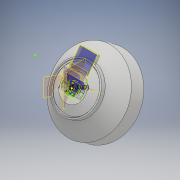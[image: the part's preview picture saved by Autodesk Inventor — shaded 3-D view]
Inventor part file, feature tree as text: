
AUTODESK INVENTOR PART (.ipt)
format: ipt  version: 2018 (Build 220112000, 112)  size: 3,336,704 bytes
history: native  units: mm
features: sketch x136, extrude x121, fillet x44, plane x12, revolve x5, hole x1, direct_edit x1, other x1
ambient origin geometry x8: Origin, YZ Plane, XZ Plane, XY Plane, X Axis, Y Axis, Z Axis, Center Point
bodies: Body1 (feature_tree)
feature tree (321):
  plane  "Work Plane5"
  sketch  "Sketch28"  dims[d118=18.7mm d119=0.0mm d120=0.9mm d121=0.0mm]
  extrude  "Extrusion21"  Depth=0.9mm TaperAngle=0.0deg
  plane  "Work Plane4"
  extrude  "Extrusion22"  Depth=3.8mm
  extrude  "Extrusion23"  Depth=46.7mm
  plane  "Work Plane3"
  hole  "Hole6"  [1 undecoded]
  extrude  "Extrusion27"  Depth=3.8mm
  extrude  "Extrusion28"  Depth=32.03mm
  extrude  "Extrusion30"  Depth=10.0mm TaperAngle=0.0deg
  extrude  "Extrusion31"  Depth=16.3mm TaperAngle=0.0deg
  sketch  "Sketch56"  dims[d188=16.3mm d189=0.0mm d190=16.3mm d191=0.0mm]
  sketch  "Sketch57"  dims[d192=16.3mm d193=0.0mm d194=16.3mm d195=0.0mm]
  extrude  "Extrusion33"  Depth=16.3mm TaperAngle=0.0deg
  extrude  "Extrusion34"  Depth=16.3mm TaperAngle=0.0deg
  extrude  "Extrusion35"  Depth=15.9mm TaperAngle=0.0deg
  extrude  "Extrusion36"  Depth=15.9mm TaperAngle=0.0deg
  extrude  "Extrusion37"  TaperAngle=90.0deg  [1 undecoded]
  extrude  "Extrusion38"  TaperAngle=0.0deg  [1 undecoded]
  extrude  "Extrusion39"  Depth=0.2mm TaperAngle=0.0deg
  extrude  "Extrusion40"  Depth=3.17mm
  extrude  "Extrusion41"  Depth=6.1mm
  sketch  "Sketch68"  dims[d251=10.0mm d252=0.0mm d253=3.91mm d254=0.0mm]
  sketch  "Sketch69"  dims[d255=0.0mm d256=0.0mm d257=3.91mm d258=0.0mm]
  extrude  "Extrusion42"  Depth=0.8mm TaperAngle=0.0deg
  extrude  "Extrusion43"  TaperAngle=0.0deg  [1 undecoded]
  extrude  "Extrusion45"  Depth=10.0mm TaperAngle=0.0deg
  extrude  "Extrusion47"  Depth=3.91mm TaperAngle=0.0deg
  extrude  "Extrusion48"  Depth=0.6mm TaperAngle=0.0deg
  extrude  "Extrusion49"  Depth=0.199mm
  direct_edit  "Direct Edit3"
  extrude  "Extrusion51"  TaperAngle=0.0deg  [1 undecoded]
  extrude  "Extrusion52"  Depth=0.7mm TaperAngle=0.0deg
  extrude  "Extrusion53"  Depth=0.09mm TaperAngle=0.0deg
  extrude  "Extrusion54"  TaperAngle=0.0deg  [1 undecoded]
  extrude  "Extrusion55"  Depth=3.9mm TaperAngle=0.0deg
  extrude  "Extrusion60"  TaperAngle=0.0deg  [1 undecoded]
  extrude  "Extrusion61"  Depth=0.657mm
  extrude  "Extrusion62"  Depth=10.0mm TaperAngle=0.0deg
  fillet  "Fillet13"  Radius=10.0mm
  extrude  "Extrusion64"  TaperAngle=0.0deg  [1 undecoded]
  extrude  "Extrusion65"  TaperAngle=0.0deg  [1 undecoded]
  extrude  "Extrusion66"  Depth=0.253mm
  extrude  "Extrusion67"  TaperAngle=0.0deg  [1 undecoded]
  fillet  "Fillet14"  [1 undecoded]
  extrude  "Extrusion68"  Depth=15.0mm
  extrude  "Extrusion69"  Depth=22.68928mm
  extrude  "Extrusion70"  TaperAngle=90.0deg  [1 undecoded]
  fillet  "Fillet15"  [1 undecoded]
  extrude  "Extrusion71"  TaperAngle=90.0deg  [1 undecoded]
  extrude  "Extrusion72"  Depth=3.490659mm
  extrude  "Extrusion73"  Depth=2.0mm TaperAngle=0.0deg
  extrude  "Extrusion74"  TaperAngle=0.0deg  [1 undecoded]
  fillet  "Fillet16"  Radius=10.0mm
  fillet  "Fillet17"  Radius=0.22mm
  extrude  "Extrusion75"  Depth=5.0mm TaperAngle=0.0deg
  plane  "Work Plane6"
  extrude  "Extrusion78"  Depth=10.0mm TaperAngle=0.0deg
  extrude  "Extrusion79"  Depth=10.0mm TaperAngle=0.0deg
  extrude  "Extrusion80"  Depth=10.0mm TaperAngle=0.0deg
  extrude  "Extrusion81"  Depth=10.0mm TaperAngle=0.0deg
  extrude  "Extrusion82"  Depth=10.0mm
  fillet  "Fillet18"  [1 undecoded]
  fillet  "Fillet19"  Radius=5.99mm
  fillet  "Fillet20"  Radius=1.49mm
  extrude  "Extrusion83"  Depth=1.77mm
  extrude  "Extrusion84"  Depth=10.0mm TaperAngle=0.0deg
  fillet  "Fillet21"  Radius=4.0mm
  extrude  "Extrusion87"  Depth=4.0mm TaperAngle=0.0deg
  plane  "Work Plane7"
  extrude  "Extrusion88"  TaperAngle=0.0deg  [1 undecoded]
  extrude  "Extrusion89"  Depth=7.0mm TaperAngle=0.0deg
  extrude  "Extrusion90"  Depth=10.0mm TaperAngle=0.0deg
  extrude  "Extrusion91"  Depth=7.0mm TaperAngle=0.0deg
  fillet  "Fillet27"  Radius=7.0mm
  extrude  "Extrusion93"  Depth=7.0mm TaperAngle=0.0deg
  extrude  "Extrusion94"  Depth=1.7mm TaperAngle=0.0deg
  fillet  "Fillet29"  [1 undecoded]
  extrude  "Extrusion95"  Depth=10.0mm TaperAngle=0.0deg
  extrude  "Extrusion97"  Depth=10.0mm TaperAngle=0.0deg
  extrude  "Extrusion98"  Depth=1.0mm TaperAngle=0.0deg
  extrude  "Extrusion99"  Depth=15.687mm
  extrude  "Extrusion100"  Depth=9.4mm
  extrude  "Extrusion101"  TaperAngle=90.0deg  [1 undecoded]
  extrude  "Extrusion102"  Depth=10.0mm TaperAngle=0.0deg
  extrude  "Extrusion104"  Depth=50.0mm TaperAngle=0.0deg
  fillet  "Fillet30"  Radius=50.0mm
  extrude  "Extrusion106"  Depth=10.0mm TaperAngle=0.0deg
  fillet  "Fillet33"  Radius=32.0mm
  fillet  "Fillet34"  Radius=9.4mm
  fillet  "Fillet35"  [1 undecoded]
  fillet  "Fillet38"  Radius=10.0mm
  extrude  "Extrusion108"  Depth=10.0mm TaperAngle=0.0deg
  extrude  "Extrusion109"  Depth=10.0mm TaperAngle=0.0deg
  extrude  "Extrusion110"  TaperAngle=0.0deg  [1 undecoded]
  extrude  "Extrusion111"  Depth=18.0mm TaperAngle=0.0deg
  extrude  "Extrusion112"  Depth=2.0mm
  sketch  "Sketch146"  dims[d571=2.0mm d572=2.0mm]
  extrude  "Extrusion113"  Depth=2.0mm
  extrude  "Extrusion114"  Depth=2.0mm
  extrude  "Extrusion115"  Depth=2.0mm
  extrude  "Extrusion116"  Depth=2.0mm
  extrude  "Extrusion118"  Depth=2.0mm
  sketch  "Sketch154"  dims[d590=2.0mm d591=4.0mm]
  extrude  "Extrusion119"  Depth=2.0mm
  extrude  "Extrusion120"  Depth=0.7mm TaperAngle=0.0deg
  extrude  "Extrusion121"  Depth=10.0mm TaperAngle=0.0deg
  extrude  "Extrusion122"  Depth=17.0mm TaperAngle=0.0deg
  extrude  "Extrusion123"  Depth=4.0mm
  extrude  "Extrusion124"  Depth=1.0mm TaperAngle=0.0deg
  extrude  "Extrusion125"  Depth=6.6945mm
  extrude  "Extrusion126"  TaperAngle=0.0deg  [1 undecoded]
  extrude  "Extrusion128"  Depth=15.2mm
  extrude  "Extrusion129"  Depth=26.0mm
  extrude  "Extrusion130"  Depth=28.5mm TaperAngle=0.0deg
  plane  "Work Plane9"
  extrude  "Extrusion133"  Depth=2.0mm
  extrude  "Extrusion134"  Depth=0.567mm
  plane  "Work Plane8"
  extrude  "Extrusion135"  Depth=0.37mm TaperAngle=0.0deg
  plane  "Work Plane2"
  revolve  "Revolution3"  [1 undecoded]
  plane  "Work Plane10"
  extrude  "Extrusion136"  Depth=2.0mm
  extrude  "Extrusion137"  Depth=2.0mm
  extrude  "Extrusion138"  TaperAngle=90.0deg  [1 undecoded]
  extrude  "Extrusion139"  Depth=0.449mm
  sketch  "Sketch184"
  plane  "Work Plane11"
  extrude  "Extrusion140"  Depth=0.526mm
  extrude  "Extrusion141"  TaperAngle=90.0deg  [1 undecoded]
  extrude  "Extrusion142"  Depth=1.0mm
  extrude  "Extrusion143"  [1 undecoded]
  revolve  "Revolution4"  [1 undecoded]
  extrude  "Extrusion145"  [1 undecoded]
  sketch  "Sketch192"
  extrude  "Extrusion147"  [1 undecoded]
  extrude  "Extrusion148"  [1 undecoded]
  extrude  "Extrusion149"  [1 undecoded]
  sketch  "Sketch198"
  sketch  "Sketch199"
  sketch  "Sketch200"
  extrude  "Extrusion150"  [1 undecoded]
  sketch  "Sketch201"
  sketch  "Sketch202"
  extrude  "Extrusion151"  [1 undecoded]
  extrude  "Extrusion152"  [1 undecoded]
  extrude  "Extrusion153"  [1 undecoded]
  extrude  "Extrusion154"  [1 undecoded]
  sketch  "Sketch207"
  extrude  "Extrusion155"  [1 undecoded]
  fillet  "Fillet39"  [1 undecoded]
  fillet  "Fillet40"  [1 undecoded]
  fillet  "Fillet41"  [1 undecoded]
  fillet  "Fillet42"  [1 undecoded]
  fillet  "Fillet43"  [1 undecoded]
  fillet  "Fillet44"  [1 undecoded]
  fillet  "Fillet45"  [1 undecoded]
  fillet  "Fillet46"  [1 undecoded]
  fillet  "Fillet47"  [1 undecoded]
  plane  "Work Plane12"
  extrude  "Extrusion156"  [1 undecoded]
  fillet  "Fillet48"  [1 undecoded]
  fillet  "Fillet49"  [1 undecoded]
  fillet  "Fillet50"  [1 undecoded]
  fillet  "Fillet51"  [1 undecoded]
  extrude  "Extrusion157"  [1 undecoded]
  fillet  "Fillet52"  [1 undecoded]
  extrude  "Extrusion158"  [1 undecoded]
  extrude  "Extrusion159"  [1 undecoded]
  extrude  "Extrusion161"  [1 undecoded]
  fillet  "Fillet53"  [1 undecoded]
  plane  "Work Plane13"
  extrude  "Extrusion163"  [1 undecoded]
  extrude  "Extrusion164"  [1 undecoded]
  extrude  "Extrusion166"  [1 undecoded]
  extrude  "Extrusion167"  [1 undecoded]
  revolve  "Revolution5"  [1 undecoded]
  extrude  "Extrusion168"  [1 undecoded]
  fillet  "Fillet54"  [1 undecoded]
  fillet  "Fillet55"  [1 undecoded]
  extrude  "Extrusion169"  [1 undecoded]
  sketch  "Sketch220"
  fillet  "Fillet56"  [1 undecoded]
  fillet  "Fillet57"  [1 undecoded]
  extrude  "Extrusion171"  [1 undecoded]
  extrude  "Extrusion172"  [1 undecoded]
  fillet  "Fillet58"  [1 undecoded]
  fillet  "Fillet59"  [1 undecoded]
  fillet  "Fillet60"  [1 undecoded]
  fillet  "Fillet61"  [1 undecoded]
  fillet  "Fillet62"  [1 undecoded]
  fillet  "Fillet63"  [1 undecoded]
  revolve  "Revolution6"  [1 undecoded]
  fillet  "Fillet64"  [1 undecoded]
  extrude  "Extrusion173"  [1 undecoded]
  fillet  "Fillet65"  [1 undecoded]
  fillet  "Fillet66"  [1 undecoded]
  revolve  "Revolution7"  [1 undecoded]
  sketch  "Sketch41"  dims[d122=0.7mm d123=0.0mm d128=3.8mm]
  sketch  "Sketch42"  dims[d129=3.8mm d130=46.7mm]
  sketch  "Sketch43"  dims[d134=3.8mm d135=4.369mm d136=5.824mm d137=2.0mm d138=14.3117mm d139=6.637mm d140=0.0mm d150=1.5mm d151=0.0mm]
  sketch  "Sketch50"  dims[d152=1.2mm d153=0.0mm d159=3.8mm]
  sketch  "Sketch51"  dims[d161=3.8mm d168=23.3333mm d173=32.03mm]
  sketch  "Sketch53"  dims[d174=16.015mm d175=10.0mm d176=0.0mm]
  sketch  "Sketch54"  dims[d179=0.0mm d180=0.0mm d186=16.3mm d187=0.0mm]
  sketch  "Sketch58"  dims[d196=15.9mm d197=0.0mm d198=15.9mm d199=0.0mm]
  sketch  "Sketch60"  dims[d200=15.9mm d201=0.0mm d202=15.9mm d203=0.0mm]
  sketch  "Sketch61"  dims[d209=17.0mm d210=90.0deg]
  sketch  "Sketch62"  dims[d211=6.0mm d212=0.0mm d213=0.0mm d214=0.0mm]
  sketch  "Sketch63"  dims[d225=6.0mm d226=0.0mm d230=0.2mm d231=0.0mm]
  sketch  "Sketch64"  dims[d232=3.17mm d233=3.17mm]
  sketch  "Sketch65"  dims[d235=19.4mm d236=6.1mm]
  sketch  "Sketch66"  dims[d237=0.8mm d238=0.0mm d239=0.8mm d240=0.0mm]
  sketch  "Sketch67"  dims[d246=9.0mm d247=10.0mm d248=10.0mm d249=0.0mm d250=0.0mm]
  sketch  "Sketch70"  dims[d267=0.0mm d268=0.0mm d269=0.6mm d270=0.0mm]
  sketch  "Sketch72"  dims[d271=0.0mm d272=0.0mm d273=0.199mm]
  sketch  "Sketch74"  dims[d276=0.0mm d277=0.0mm d278=0.0mm d279=0.0mm]
  sketch  "Sketch75"  dims[d280=0.7mm d281=0.0mm d282=0.7mm d283=0.0mm]
  sketch  "Sketch76"  dims[d284=3.64mm d285=0.09mm d286=0.0mm]
  sketch  "Sketch79"  dims[d287=0.09mm d288=0.0mm d289=0.0mm d290=0.0mm]
  sketch  "Sketch80"  dims[d291=0.356mm d292=3.9mm d293=0.0mm]
  sketch  "Sketch81"  dims[d294=3.9mm d295=0.0mm d296=0.0mm d297=0.0mm]
  sketch  "Sketch82"  dims[d298=3.9mm d299=0.0mm d300=0.657mm]
  sketch  "Sketch83"  dims[d301=0.886mm d302=3.9mm d303=0.0mm d313=10.0mm d314=0.0mm]
  sketch  "Sketch89"  dims[d315=10.0mm d316=0.0mm d317=0.0mm d318=0.0mm]
  sketch  "Sketch90"  dims[d319=10.0mm d320=0.0mm d321=0.0mm d322=0.0mm]
  sketch  "Sketch91"  dims[d323=0.467mm d324=0.253mm]
  sketch  "Sketch93"  dims[d325=0.195mm d326=0.0mm d327=0.0mm d328=90.0deg]
  sketch  "Sketch94"  dims[d329=90.0deg d330=15.0mm]
  sketch  "Sketch95"  dims[d332=11.0mm d333=22.68928mm]
  sketch  "Sketch96"  dims[d335=90.0deg d336=90.0deg d337=0.0mm d338=0.0mm]
  sketch  "Sketch97"  dims[d344=0.954mm d350=90.0deg]
  sketch  "Sketch98"  dims[d351=3.490659mm d352=3.490659mm]
  sketch  "Sketch99"  dims[d353=6.0mm d354=0.0mm d363=2.0mm d364=0.0mm]
  sketch  "Sketch100"  dims[d365=2.0mm d366=0.0mm d374=0.0mm d375=0.0mm d376=10.0mm d377=0.0mm d378=0.22mm]
  sketch  "Sketch101"  dims[d381=5.0mm d382=0.0mm d383=5.0mm d384=0.0mm]
  sketch  "Sketch102"  dims[d386=3.8mm d397=10.0mm d398=0.0mm]
  sketch  "Sketch103"  dims[d401=0.3mm d402=0.0mm d403=10.0mm d404=0.0mm]
  sketch  "Sketch104"  dims[d405=10.0mm d406=0.0mm d407=10.0mm d408=0.0mm]
  sketch  "Sketch106"  dims[d409=10.0mm d410=0.0mm d411=10.0mm d412=0.0mm]
  sketch  "Sketch107"  dims[d415=10.0mm d416=0.0mm d419=0.865mm d421=0.0mm d422=0.0mm d424=5.99mm d425=1.49mm]
  sketch  "Sketch108"  dims[d426=0.859mm d431=1.77mm]
  sketch  "Sketch109"  dims[d432=10.0mm d433=0.0mm d434=4.0mm d435=0.0mm d436=4.0mm d437=0.0mm]
  sketch  "Sketch110"  dims[d438=4.0mm d439=0.0mm d440=4.0mm d441=0.0mm]
  sketch  "Sketch113"  dims[d442=0.0mm d443=0.0mm d444=0.0mm d445=0.0mm]
  sketch  "Sketch114"  dims[d446=1.0mm d447=0.0mm d448=7.0mm d449=0.0mm]
  sketch  "Sketch117"  dims[d452=7.0mm d453=0.0mm d454=10.0mm d455=0.0mm]
  sketch  "Sketch118"  dims[d456=0.0mm d457=0.0mm d458=7.0mm d459=0.0mm d460=7.0mm d461=0.0mm]
  sketch  "Sketch119"  dims[d462=0.0mm d463=0.0mm d464=7.0mm d465=0.0mm]
  sketch  "Sketch120"  dims[d466=1.7mm d467=0.0mm d468=1.7mm d469=0.0mm d483=0.0mm d484=0.0mm]
  sketch  "Sketch121"  dims[d485=0.0mm d486=0.0mm d487=10.0mm d488=0.0mm]
  sketch  "Sketch123"  dims[d496=10.0mm d497=0.0mm d498=10.0mm d499=0.0mm]
  sketch  "Sketch124"  dims[d500=31.5mm d501=1.0mm d502=0.0mm]
  sketch  "Sketch126"  dims[d508=-1.0mm d509=15.687mm]
  sketch  "Sketch128"  dims[d510=90.0deg d514=9.4mm]
  sketch  "Sketch129"  dims[d516=7.0mm d519=90.0deg]
  sketch  "Sketch130"  dims[d520=2.75mm d521=0.0mm d522=10.0mm d523=0.0mm]
  sketch  "Sketch131"  dims[d524=7.0mm d525=0.0mm d527=50.0mm d528=0.0mm d529=50.0mm d530=0.0mm]
  sketch  "Sketch132"  dims[d531=50.0mm d532=0.0mm d533=50.0mm d534=0.0mm d535=32.0mm d536=0.0mm d537=9.4mm d538=7.0mm d539=90.0deg d542=10.0mm d543=0.0mm]
  sketch  "Sketch133"  dims[d546=10.0mm d547=0.0mm d548=10.0mm d549=0.0mm]
  sketch  "Sketch135"  dims[d550=31.0mm d551=0.0mm d552=10.0mm d553=0.0mm]
  sketch  "Sketch137"  dims[d554=5.5mm d555=0.0mm d556=0.0mm d557=0.0mm]
  sketch  "Sketch141"  dims[d558=5.5mm d559=0.0mm d560=18.0mm d561=0.0mm]
  sketch  "Sketch142"  dims[d562=18.0mm d563=0.0mm d564=2.0mm]
  sketch  "Sketch143"  dims[d565=2.0mm d566=2.0mm]
  sketch  "Sketch144"  dims[d567=2.0mm d568=2.0mm]
  sketch  "Sketch145"  dims[d569=2.0mm d570=2.0mm]
  sketch  "Sketch147"  dims[d573=0.0mm d574=0.0mm d575=2.0mm]
  sketch  "Sketch148"  dims[d576=2.0mm d577=2.0mm]
  sketch  "Sketch149"  dims[d578=2.0mm d579=0.7mm d580=0.0mm]
  sketch  "Sketch150"  dims[d581=2.0mm d582=10.0mm d583=0.0mm]
  sketch  "Sketch153"  dims[d584=2.15mm d585=0.0mm d588=17.0mm d589=0.0mm]
  sketch  "Sketch156"  dims[d594=3.0mm d595=0.0mm d596=1.0mm d597=0.0mm]
  sketch  "Sketch157"  dims[d598=7.23mm d599=6.6945mm]
  sketch  "Sketch161"  dims[d602=31.423mm d603=0.0mm d604=0.0mm]
  sketch  "Sketch162"  dims[d605=1.0mm d606=0.0mm d607=15.2mm]
  sketch  "Sketch163"  dims[d609=5.093mm d611=26.0mm]
  sketch  "Sketch164"  dims[d615=90.0deg d616=28.5mm d617=0.0mm]
  sketch  "Sketch165"  dims[d618=2.0mm d619=2.0mm]
  sketch  "Sketch166"  dims[d620=2.235mm d621=0.0mm d624=0.567mm]
  sketch  "Sketch169"  dims[d625=0.682mm d626=0.37mm d627=0.0mm]
  sketch  "Sketch170"  dims[d628=1.2mm d629=0.0mm d630=2.0mm]
  sketch  "Sketch171"  dims[d631=2.0mm d632=2.0mm]
  sketch  "Sketch174"  dims[d633=2.0mm d634=2.0mm]
  sketch  "Sketch175"  dims[d635=2.0mm d639=90.0deg]
  sketch  "Sketch176"  dims[d640=90.0deg d641=0.449mm]
  sketch  "Sketch179"  dims[d642=1.2mm d643=0.0mm d644=0.526mm]
  sketch  "Sketch180"  dims[d645=2.0mm d646=90.0deg]
  sketch  "Sketch181"  dims[d21=1.0mm d22=1.0mm]
  sketch  "Sketch182"
  sketch  "Sketch183"
  sketch  "Sketch185"
  sketch  "Sketch186"
  sketch  "Sketch187"
  sketch  "Sketch188"
  sketch  "Sketch190"
  sketch  "Sketch193"
  sketch  "Sketch194"
  sketch  "Sketch195"
  sketch  "Sketch204"
  sketch  "Sketch205"
  sketch  "Sketch206"
  sketch  "Sketch208"
  sketch  "Sketch209"
  sketch  "Sketch210"
  sketch  "Sketch211"
  sketch  "Sketch212"
  sketch  "Sketch213"
  sketch  "Sketch214"
  sketch  "Sketch215"
  sketch  "Sketch216"
  sketch  "Sketch217"
  sketch  "Sketch218"
  sketch  "Sketch219"
  sketch  "Sketch221"
  sketch  "Sketch222"
  sketch  "Sketch223"
  sketch  "Sketch224"
  other  "Scale3"
note: 82 required parameter values undecoded (feature->parameter linkage not recoverable at this tier; creation-order binding heuristic only, values carry confidence <= 0.55)